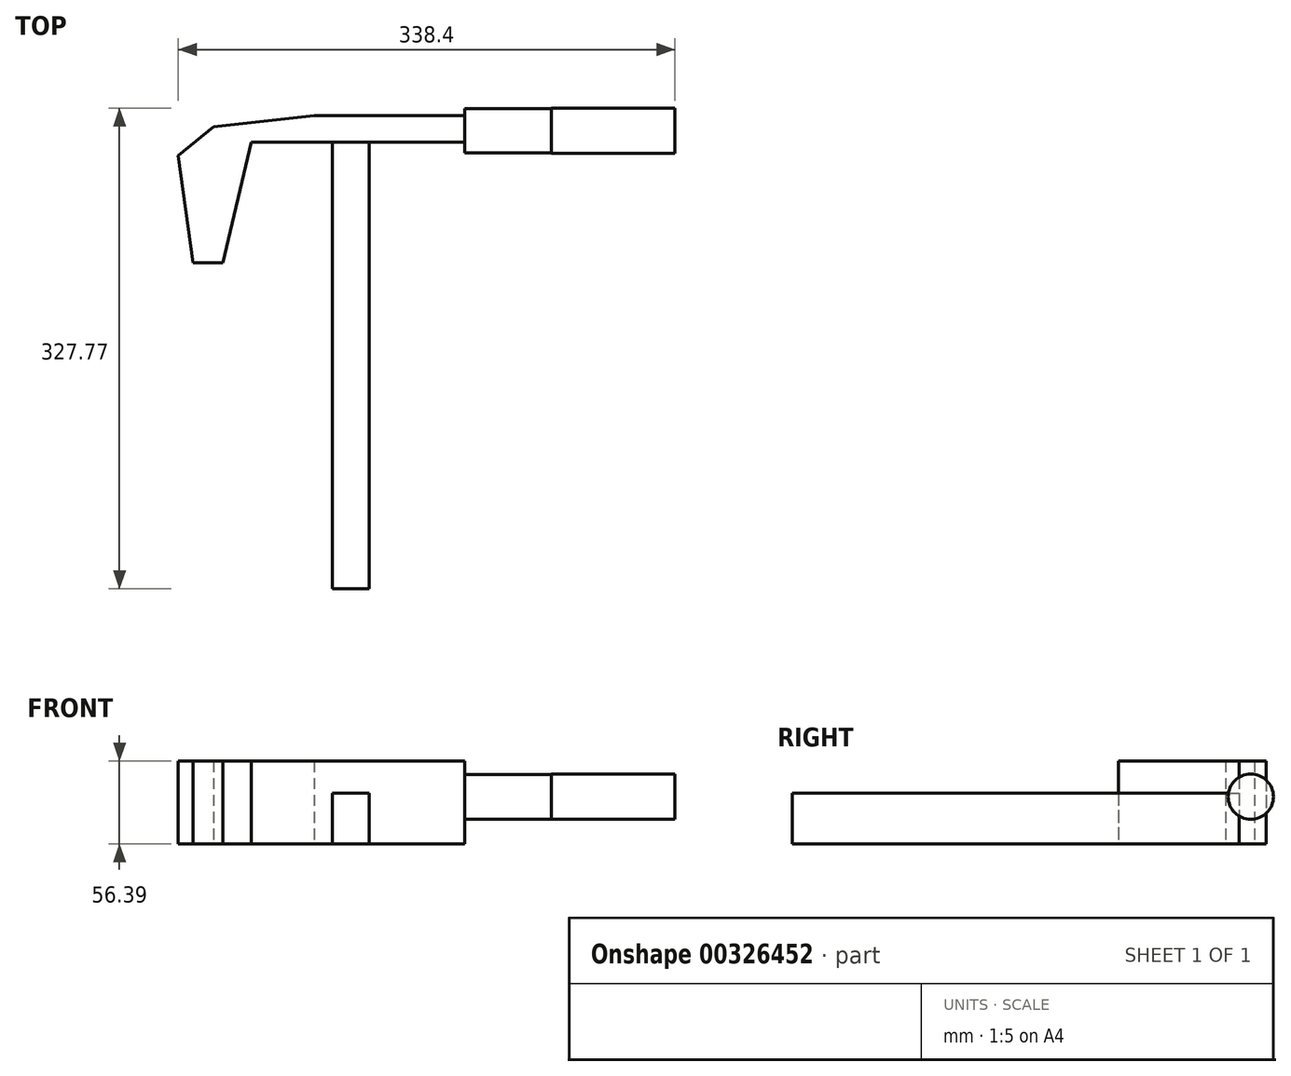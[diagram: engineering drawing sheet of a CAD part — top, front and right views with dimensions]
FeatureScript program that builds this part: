
annotation { "Feature Type Name" : "Feature", "Feature Type Description" : "" }
export const myFeature = defineFeature(function(context is Context, id is Id, definition is map)
    precondition{}
    {
        {
            var Q0;
            Q0=qCreatedBy(makeId("Top.planeOp"),FACE);
            var sketch = newSketch(context, id + "F0", { "sketchPlane" : qUnion([Q0])});
            skLineSegment(sketch, "E0.bottom", {"start": v(-71.22, 46.14) * mm, "end": v(31.19, 46.14) * mm});
            skLineSegment(sketch, "E0.top", {"start": v(-71.22, 28) * mm, "end": v(31.19, 28) * mm});
            skLineSegment(sketch, "E0.left", {"start": v(-71.22, 46.14) * mm, "end": v(-71.22, 28) * mm});
            skLineSegment(sketch, "E0.right", {"start": v(31.19, 46.14) * mm, "end": v(31.19, 28) * mm});
            skLineSegment(sketch, "E1", {"start": v(-71.22, 28) * mm, "end": v(-114.27, 28) * mm});
            skLineSegment(sketch, "E2", {"start": v(-114.27, 28) * mm, "end": v(-133.52, -54.35) * mm});
            skLineSegment(sketch, "E3", {"start": v(-133.52, -54.35) * mm, "end": v(-153.93, -54.35) * mm});
            skLineSegment(sketch, "E4", {"start": v(-153.93, -54.35) * mm, "end": v(-163.96, 18.77) * mm});
            skLineSegment(sketch, "E5", {"start": v(-163.96, 18.77) * mm, "end": v(-140.08, 38.41) * mm});
            skLineSegment(sketch, "E6", {"start": v(-140.08, 38.41) * mm, "end": v(-71.22, 46.14) * mm});
            skSolve(sketch);
        }
        {
            var Q0;
            Q0 = qSketchRegion(id + "F0", true);
            extrude(context, id + "F1", {"entities" : qUnion([Q0]), "depth" : 56.4 * mm});
        }
        {
            var Q0;
            Q0=makeQuery(id+"F1.opExtrude","SWEPT_FACE",FACE,{"disambiguationData":[OSD([sQuery(id+"F0.wireOp",EDGE,"E0.top"),sQuery(id+"F0.wireOp",EDGE,"E1")])]});
            var sketch = newSketch(context, id + "F2", { "sketchPlane" : qUnion([Q0])});
            skLineSegment(sketch, "E7.bottom", {"start": v(-59.1, 34.54) * mm, "end": v(-34.03, 34.54) * mm});
            skLineSegment(sketch, "E7.top", {"start": v(-59.1, 0) * mm, "end": v(-34.03, 0) * mm});
            skLineSegment(sketch, "E7.left", {"start": v(-59.1, 34.54) * mm, "end": v(-59.1, 0) * mm});
            skLineSegment(sketch, "E7.right", {"start": v(-34.03, 34.54) * mm, "end": v(-34.03, 0) * mm});
            skSolve(sketch);
        }
        {
            var Q0;
            Q0 = qSketchRegion(id + "F2", true);
            extrude(context, id + "F3", {"entities" : qUnion([Q0]), "operationType" : NewBodyOperationType.ADD, "depth" : 304.55 * mm});
        }
        {
            var Q0;
            Q0=makeQuery(id+"F1.opExtrude","SWEPT_FACE",FACE,{"disambiguationData":[OSD([sQuery(id+"F0.wireOp",EDGE,"E0.right")])]});
            var sketch = newSketch(context, id + "F4", { "sketchPlane" : qUnion([Q0])});
            skCircle(sketch, "E8", {"center": v(35.8, 32.16) * mm, "radius": 15.23 * mm});
            skSolve(sketch);
        }
        {
            var Q0;
            Q0 = qSketchRegion(id + "F4", true);
            extrude(context, id + "F5", {"entities" : qUnion([Q0]), "operationType" : NewBodyOperationType.ADD, "depth" : 58.93 * mm});
        }
        {
            var Q0;
            Q0=makeQuery(id+"F5.opExtrude","CAP_FACE",FACE,{"disambiguationData":[OSD([sQuery(id+"F4.wireOp",EDGE,"E8")])],"isStart":false});
            var sketch = newSketch(context, id + "F6", { "sketchPlane" : qUnion([Q0])});
            skCircle(sketch, "E9", {"center": v(35.8, 32.16) * mm, "radius": 15.43 * mm});
            skSolve(sketch);
        }
        {
            var Q0;
            Q0 = qSketchRegion(id + "F6", true);
            extrude(context, id + "F7", {"entities" : qUnion([Q0]), "operationType" : NewBodyOperationType.ADD, "depth" : 84.33 * mm});
        }
    });
